# Revit family: Bomsystem2 sammansatt
name_source: partatom
category: Generic Models
revit_build: Autodesk Revit 2017 (Build: 20160225_1515(x64)
units: mm (PartAtom-declared; Revit-internal decimal feet)

## family parameters
Always vertical = Yes
Can host rebar = No
Cut with Voids When Loaded = No
Part Type = Normal
Room Calculation Point = No
Round Connector Dimension = Use Diameter
Shared = No
Work Plane-Based = No

## types (4) — shared parameters
Height = 7000 mm  [stored 22.9659 ft]
Height_stolpe = 6940 mm  [stored 22.769 ft]
Height_stolpe2 = 5800 mm  [stored 19.0289 ft]
Manufacturer = Saxi Vägg AB
Model = Saxi Bomsystem 1
URL = www.saxi.se
to_middle_support = 3500 mm  [stored 11.4829 ft]

## per-type parameters (varying)
| type | 2 | H | V |
| Saxi Bomsystem 3 V | No | No | Yes |
| Saxi Bomsystem 3 H | No | Yes | No |
| Saxi Bomsystem 4 V | Yes | No | Yes |
| Saxi Bomsystem 4 H | Yes | Yes | No |

note: [stored X ft] marks values corroborated as IEEE doubles in the binary element streams (Revit-internal decimal feet)

## geometry (parser evidence)
native form markers: Sweep x44
no freeform markers — native parametric forms only
